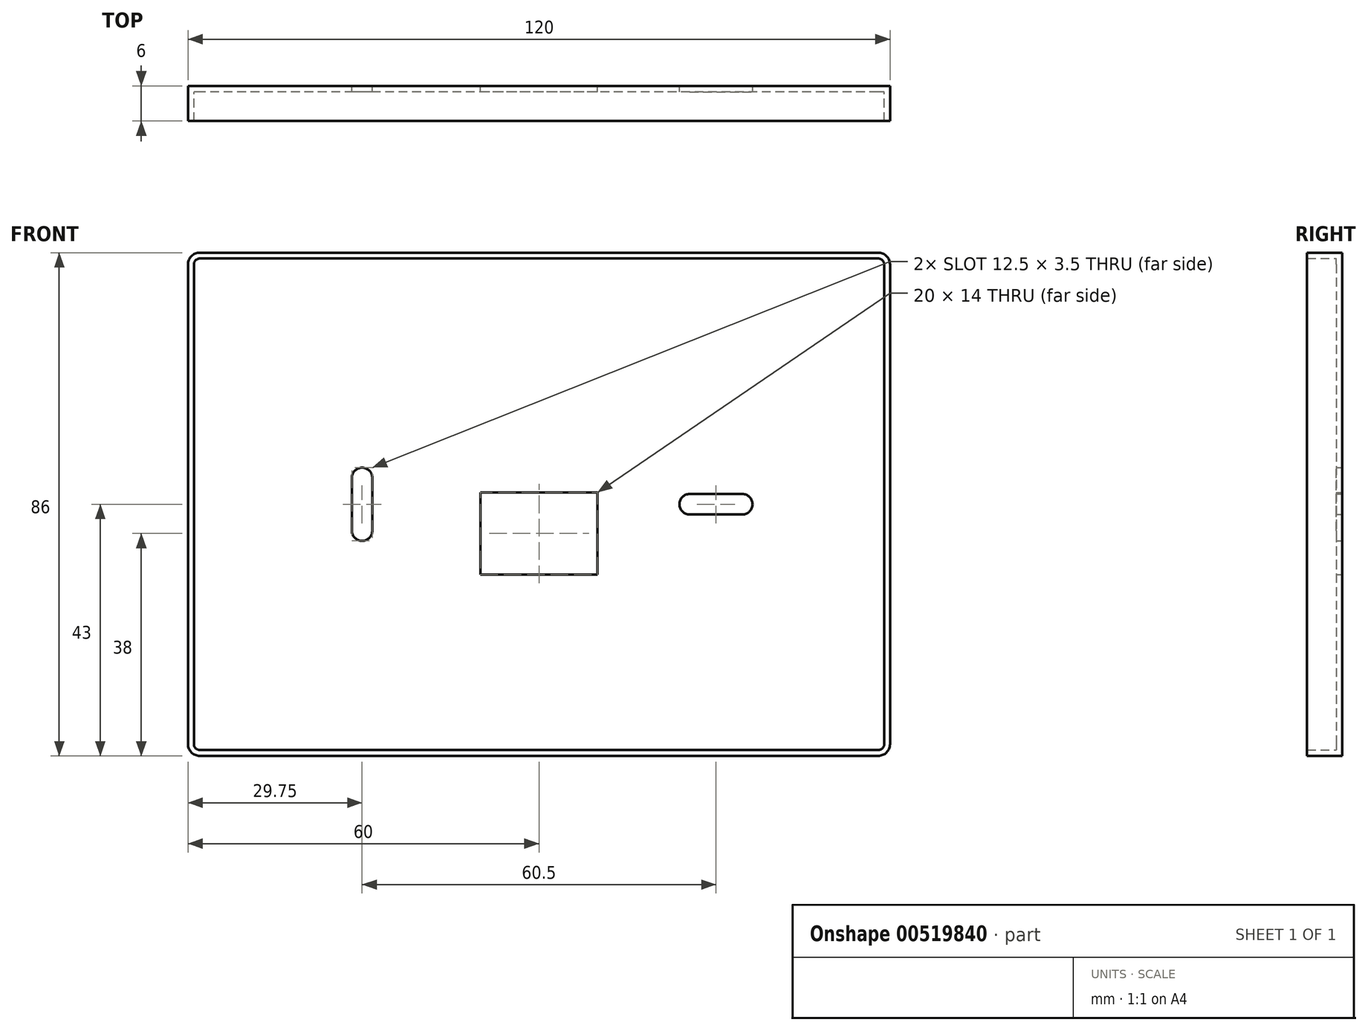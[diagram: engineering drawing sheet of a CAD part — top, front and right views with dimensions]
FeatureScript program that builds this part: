
annotation { "Feature Type Name" : "Feature", "Feature Type Description" : "" }
export const myFeature = defineFeature(function(context is Context, id is Id, definition is map)
    precondition{}
    {
        {
            var Q0;
            Q0=qCreatedBy(makeId("Front.planeOp"),FACE);
            var sketch = newSketch(context, id + "F0", { "sketchPlane" : qUnion([Q0])});
            skLineSegment(sketch, "E0.bottom", {"start": v(60, 43) * mm, "end": v(-60, 43) * mm});
            skLineSegment(sketch, "E0.top", {"start": v(60, -43) * mm, "end": v(-60, -43) * mm});
            skLineSegment(sketch, "E0.left", {"start": v(60, 43) * mm, "end": v(60, -43) * mm});
            skLineSegment(sketch, "E0.right", {"start": v(-60, 43) * mm, "end": v(-60, -43) * mm});
            skPoint(sketch, "E0.middle", {"position": v(0, 0) * mm});
            skLineSegment(sketch, "E1.bottom", {"start": v(10, 2) * mm, "end": v(-10, 2) * mm});
            skLineSegment(sketch, "E1.top", {"start": v(10, -12) * mm, "end": v(-10, -12) * mm});
            skLineSegment(sketch, "E1.left", {"start": v(10, 2) * mm, "end": v(10, -12) * mm});
            skLineSegment(sketch, "E1.right", {"start": v(-10, 2) * mm, "end": v(-10, -12) * mm});
            skPoint(sketch, "E1.middle", {"position": v(0, -5) * mm});
            skLineSegment(sketch, "E2", {"start": v(25.75, 0) * mm, "end": v(34.75, 0) * mm, "construction": true});
            skArc(sketch, "E3.0.startCap", {"start": v(25.75, -1.75) * mm, "mid": v(24, 0) * mm, "end": v(25.75, 1.75) * mm});
            skArc(sketch, "E3.0.endCap", {"start": v(34.75, 1.75) * mm, "mid": v(36.5, 0) * mm, "end": v(34.75, -1.75) * mm});
            skLineSegment(sketch, "E3.0.left", {"start": v(25.75, 1.75) * mm, "end": v(34.75, 1.75) * mm});
            skLineSegment(sketch, "E3.0.right", {"start": v(25.75, -1.75) * mm, "end": v(34.75, -1.75) * mm});
            skLineSegment(sketch, "E4", {"start": v(-30.25, -4.5) * mm, "end": v(-30.25, 4.5) * mm, "construction": true});
            skPoint(sketch, "E5", {"position": v(-30.25, 0) * mm});
            skPoint(sketch, "E6", {"position": v(30.25, 0) * mm});
            skArc(sketch, "E7.0.startCap", {"start": v(-28.5, -4.5) * mm, "mid": v(-30.25, -6.25) * mm, "end": v(-32, -4.5) * mm});
            skArc(sketch, "E7.0.endCap", {"start": v(-32, 4.5) * mm, "mid": v(-30.25, 6.25) * mm, "end": v(-28.5, 4.5) * mm});
            skLineSegment(sketch, "E7.0.left", {"start": v(-32, -4.5) * mm, "end": v(-32, 4.5) * mm});
            skLineSegment(sketch, "E7.0.right", {"start": v(-28.5, -4.5) * mm, "end": v(-28.5, 4.5) * mm});
            skSolve(sketch);
        }
        {
            var Q0;
            Q0=makeQuery(id+"F0.imprint","IMPRINT",FACE,{"disambiguationData":[TD([[makeQuery(id+"F0.imprint","IMPRINT",EDGE,{"derivedFrom":sQuery(id+"F0.wireOp",EDGE,"E0.bottom")}),1.0]])]});
            extrude(context, id + "F1", {"entities" : qUnion([Q0]), "depth" : 6 * mm, "offsetDistance" : 25 * mm});
        }
        {
            var Q0;
            Q0=makeQuery(id+"F1.opExtrude","SWEPT_EDGE",EDGE,{"disambiguationData":[OSD([sQuery(id+"F0.wireOp",EDGE,"E0.top"),sQuery(id+"F0.wireOp",EDGE,"E0.right")])]});
            var Q1;
            Q1=makeQuery(id+"F1.opExtrude","SWEPT_EDGE",EDGE,{"disambiguationData":[OSD([sQuery(id+"F0.wireOp",EDGE,"E0.bottom"),sQuery(id+"F0.wireOp",EDGE,"E0.right")])]});
            var Q2;
            Q2=makeQuery(id+"F1.opExtrude","SWEPT_EDGE",EDGE,{"disambiguationData":[OSD([sQuery(id+"F0.wireOp",EDGE,"E0.bottom"),sQuery(id+"F0.wireOp",EDGE,"E0.left")])]});
            var Q3;
            Q3=makeQuery(id+"F1.opExtrude","SWEPT_EDGE",EDGE,{"disambiguationData":[OSD([sQuery(id+"F0.wireOp",EDGE,"E0.top"),sQuery(id+"F0.wireOp",EDGE,"E0.left")])]});
            fillet(context, id + "F2", {"entities" : qUnion([Q0, Q1, Q2, Q3]), "radius" : 2 * mm, "tangentPropagation" : true, "allowEdgeOverflow" : false});
        }
        {
            var Q0;
            Q0=makeQuery(id+"F1.opExtrude","SWEPT_FACE",FACE,{"disambiguationData":[OSD([sQuery(id+"F0.wireOp",EDGE,"E7.0.right")])]});
            var Q1;
            Q1=makeQuery(id+"F1.opExtrude","SWEPT_FACE",FACE,{"disambiguationData":[OSD([sQuery(id+"F0.wireOp",EDGE,"E7.0.endCap")])]});
            var Q2;
            Q2=makeQuery(id+"F1.opExtrude","SWEPT_FACE",FACE,{"disambiguationData":[OSD([sQuery(id+"F0.wireOp",EDGE,"E7.0.left")])]});
            var Q3;
            Q3=makeQuery(id+"F1.opExtrude","SWEPT_FACE",FACE,{"disambiguationData":[OSD([sQuery(id+"F0.wireOp",EDGE,"E7.0.startCap")])]});
            var Q4;
            Q4=makeQuery(id+"F1.opExtrude","SWEPT_FACE",FACE,{"disambiguationData":[OSD([sQuery(id+"F0.wireOp",EDGE,"E1.left")])]});
            var Q5;
            Q5=makeQuery(id+"F1.opExtrude","SWEPT_FACE",FACE,{"disambiguationData":[OSD([sQuery(id+"F0.wireOp",EDGE,"E1.bottom")])]});
            var Q6;
            Q6=makeQuery(id+"F1.opExtrude","CAP_FACE",FACE,{"disambiguationData":[OSD([sQuery(id+"F0.wireOp",EDGE,"E0.bottom"),sQuery(id+"F0.wireOp",EDGE,"E0.top"),sQuery(id+"F0.wireOp",EDGE,"E0.left"),sQuery(id+"F0.wireOp",EDGE,"E0.right"),sQuery(id+"F0.wireOp",EDGE,"E1.bottom"),sQuery(id+"F0.wireOp",EDGE,"E1.top"),sQuery(id+"F0.wireOp",EDGE,"E1.left"),sQuery(id+"F0.wireOp",EDGE,"E1.right"),sQuery(id+"F0.wireOp",EDGE,"E3.0.startCap"),sQuery(id+"F0.wireOp",EDGE,"E3.0.endCap"),sQuery(id+"F0.wireOp",EDGE,"E3.0.left"),sQuery(id+"F0.wireOp",EDGE,"E3.0.right"),sQuery(id+"F0.wireOp",EDGE,"E7.0.startCap"),sQuery(id+"F0.wireOp",EDGE,"E7.0.endCap"),sQuery(id+"F0.wireOp",EDGE,"E7.0.left"),sQuery(id+"F0.wireOp",EDGE,"E7.0.right")])],"isStart":false});
            var Q7;
            Q7=makeQuery(id+"F1.opExtrude","SWEPT_FACE",FACE,{"disambiguationData":[OSD([sQuery(id+"F0.wireOp",EDGE,"E1.top")])]});
            var Q8;
            Q8=makeQuery(id+"F1.opExtrude","SWEPT_FACE",FACE,{"disambiguationData":[OSD([sQuery(id+"F0.wireOp",EDGE,"E1.right")])]});
            var Q9;
            Q9=makeQuery(id+"F1.opExtrude","SWEPT_FACE",FACE,{"disambiguationData":[OSD([sQuery(id+"F0.wireOp",EDGE,"E3.0.left")])]});
            var Q10;
            Q10=makeQuery(id+"F1.opExtrude","SWEPT_FACE",FACE,{"disambiguationData":[OSD([sQuery(id+"F0.wireOp",EDGE,"E3.0.endCap")])]});
            var Q11;
            Q11=makeQuery(id+"F1.opExtrude","SWEPT_FACE",FACE,{"disambiguationData":[OSD([sQuery(id+"F0.wireOp",EDGE,"E3.0.startCap")])]});
            var Q12;
            Q12=makeQuery(id+"F1.opExtrude","SWEPT_FACE",FACE,{"disambiguationData":[OSD([sQuery(id+"F0.wireOp",EDGE,"E3.0.right")])]});
            var Q13;
            Q13=makeQuery(id+"F1.opExtrude","SWEPT_BODY",BODY,{"disambiguationData":[OSD([sQuery(id+"F0.wireOp",EDGE,"E0.bottom"),sQuery(id+"F0.wireOp",EDGE,"E0.top"),sQuery(id+"F0.wireOp",EDGE,"E0.left"),sQuery(id+"F0.wireOp",EDGE,"E0.right"),sQuery(id+"F0.wireOp",EDGE,"E1.bottom"),sQuery(id+"F0.wireOp",EDGE,"E1.top"),sQuery(id+"F0.wireOp",EDGE,"E1.left"),sQuery(id+"F0.wireOp",EDGE,"E1.right"),sQuery(id+"F0.wireOp",EDGE,"E3.0.startCap"),sQuery(id+"F0.wireOp",EDGE,"E3.0.endCap"),sQuery(id+"F0.wireOp",EDGE,"E3.0.left"),sQuery(id+"F0.wireOp",EDGE,"E3.0.right"),sQuery(id+"F0.wireOp",EDGE,"E7.0.startCap"),sQuery(id+"F0.wireOp",EDGE,"E7.0.endCap"),sQuery(id+"F0.wireOp",EDGE,"E7.0.left"),sQuery(id+"F0.wireOp",EDGE,"E7.0.right")])]});
            shell(context, id + "F3", {"entities" : qUnion([Q0, Q1, Q2, Q3, Q4, Q5, Q6, Q7, Q8, Q9, Q10, Q11, Q12]), "parts" : qUnion([Q13]), "thickness" : 1 * mm});
        }
    });
